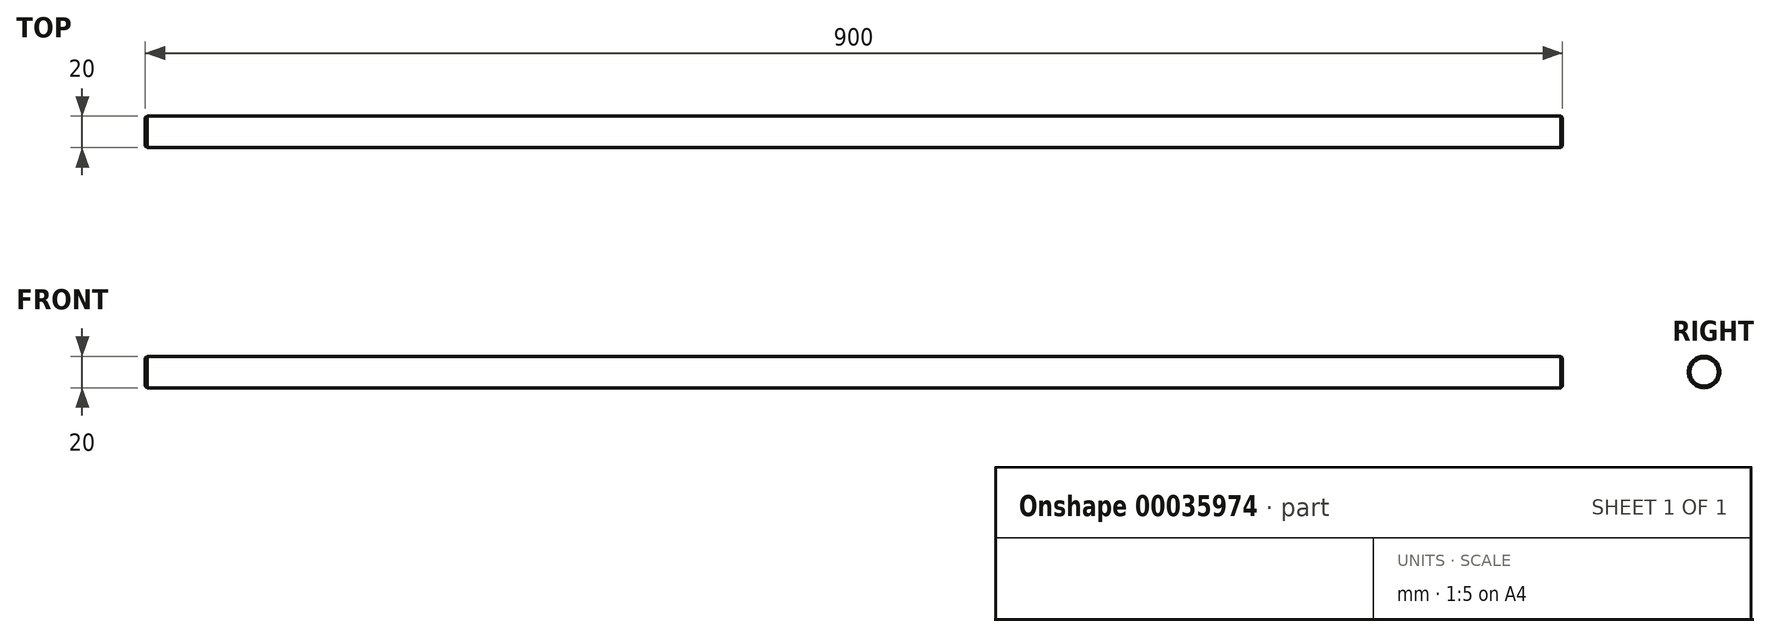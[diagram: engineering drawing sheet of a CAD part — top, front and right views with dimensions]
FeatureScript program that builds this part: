
annotation { "Feature Type Name" : "Feature", "Feature Type Description" : "" }
export const myFeature = defineFeature(function(context is Context, id is Id, definition is map)
    precondition{}
    {
        {
            var Q0;
            Q0=qCreatedBy(makeId("Right.planeOp"),FACE);
            var sketch = newSketch(context, id + "F0", { "sketchPlane" : qUnion([Q0])});
            skCircle(sketch, "E0", {"center": v(0, 0) * mm, "radius": 10 * mm});
            skSolve(sketch);
        }
        {
            var Q0;
            Q0=makeQuery(id+"F0.imprint","IMPRINT",FACE,{"disambiguationData":[TD([[makeQuery(id+"F0.imprint","IMPRINT",EDGE,{"derivedFrom":sQuery(id+"F0.wireOp",EDGE,"E0")}),1.0]])]});
            extrude(context, id + "F1", {"entities" : qUnion([Q0]), "depth" : 900 * mm});
        }
        {
            var Q0;
            Q0=makeQuery(id+"F1.opExtrude","CAP_EDGE",EDGE,{"disambiguationData":[OSD([sQuery(id+"F0.wireOp",EDGE,"E0")])],"isStart":true});
            var Q1;
            Q1=makeQuery(id+"F1.opExtrude","CAP_EDGE",EDGE,{"disambiguationData":[OSD([sQuery(id+"F0.wireOp",EDGE,"E0")])],"isStart":false});
            chamfer(context, id + "F2", {"entities" : qUnion([Q0, Q1]), "width" : 1 * mm, "tangentPropagation" : true});
        }
    });
